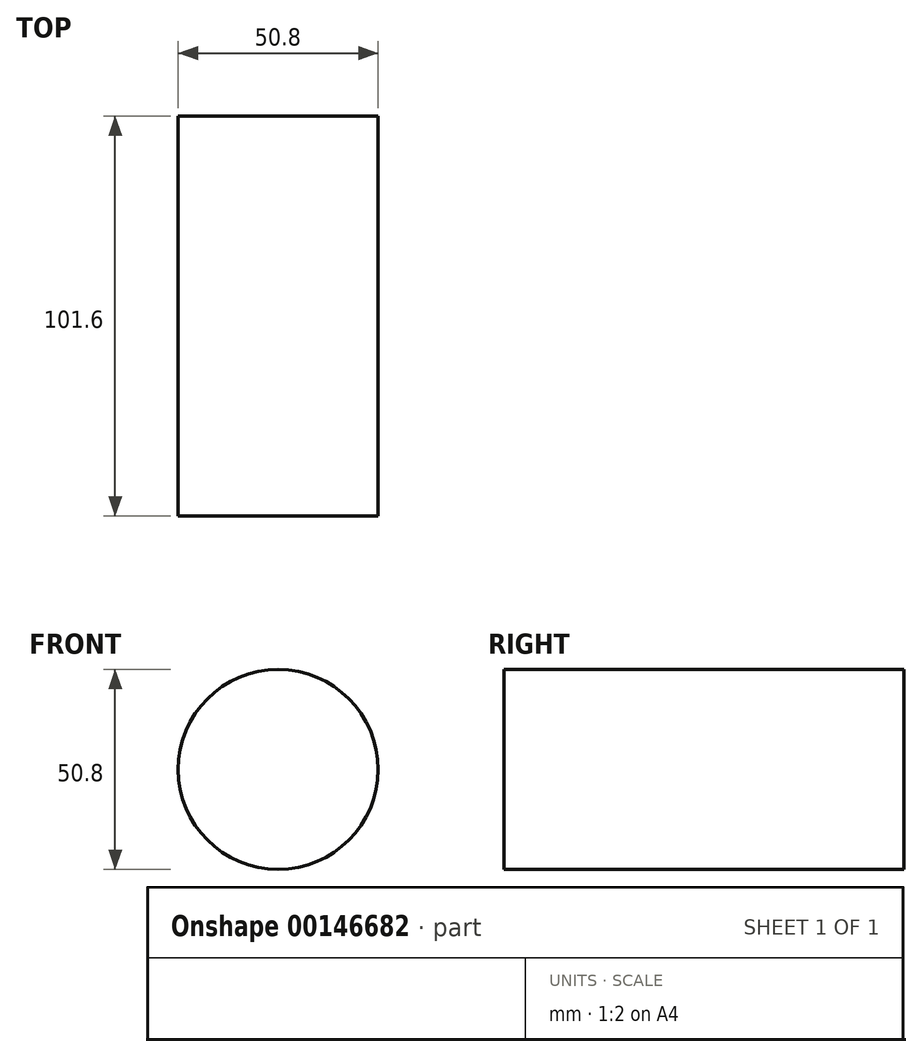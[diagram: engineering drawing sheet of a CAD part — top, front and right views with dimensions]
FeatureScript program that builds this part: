
annotation { "Feature Type Name" : "Feature", "Feature Type Description" : "" }
export const myFeature = defineFeature(function(context is Context, id is Id, definition is map)
    precondition{}
    {
        {
            var Q0;
            Q0=qCreatedBy(makeId("Front.planeOp"),FACE);
            var sketch = newSketch(context, id + "F0", { "sketchPlane" : qUnion([Q0])});
            skCircle(sketch, "E0", {"center": v(0, 0) * mm, "radius": 25.4 * mm});
            skSolve(sketch);
        }
        {
            var Q0;
            Q0=makeQuery(id+"F0.imprint","IMPRINT",FACE,{"disambiguationData":[TD([[makeQuery(id+"F0.imprint","IMPRINT",EDGE,{"derivedFrom":sQuery(id+"F0.wireOp",EDGE,"E0")}),1.0]])]});
            extrude(context, id + "F1", {"entities" : qUnion([Q0]), "endBound" : BoundingType.SYMMETRIC, "depth" : 101.6 * mm});
        }
    });
